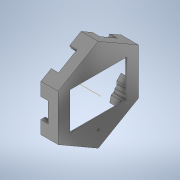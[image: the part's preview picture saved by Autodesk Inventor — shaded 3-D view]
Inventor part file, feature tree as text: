
AUTODESK INVENTOR PART (.ipt)
format: ipt  version: 2020 (Build 240168000, 168)  size: 441,344 bytes
history: native  units: mm
features: extrude x7, sketch x3, pattern_circular x1, chamfer x1, fillet x1, hole x1
ambient origin geometry x8: Origin, YZ Plane, XZ Plane, XY Plane, X Axis, Y Axis, Z Axis, Center Point
bodies: Body1 (feature_tree)
feature tree (14):
  sketch  "Sketch6"  dims[d44=97.0mm d72=6.5mm]
  extrude  "Fronte"  Depth=6.5mm
  extrude  "Esterno"  Depth=1.0mm TaperAngle=0.0deg
  extrude  "Strip"  Depth=6.5mm
  extrude  "Passacavi"  Depth=30.0mm
  extrude  "ScavoStrip"  Depth=2.0mm
  extrude  "ScreenDist0.8"  Depth=2.0mm
  extrude  "SupportoViti"  Depth=2.0mm
  pattern_circular  "RipetizioneSupports"  [2 undecoded]
  chamfer  "Smusso interno"  Distance=2.5mm
  fillet  "RaccordoSupports"  Radius=26.0mm
  hole  "ForoPulsante"  [1 undecoded]
  sketch  "Sketch7"  dims[d77=140.0mm d85=1.0mm d86=0.0mm]
  sketch  "Sketch9"  dims[d87=15.0mm d88=6.5mm d89=30.0mm d91=2.0mm d92=2.0mm d95=1.25mm d96=26.0mm d97=2.5mm d98=26.0mm d99=135.0deg d100=0.0mm d101=25.0mm d102=0.0mm d103=10.0mm d104=0.0mm d105=11.0mm d106=0.0mm d107=5.0mm d108=0.0mm d111=0.8mm d112=0.0mm d114=1.7mm d115=23.0mm d116=0.0mm d117=3.0mm d118=60.0mm d119=360.0deg d121=3.0mm d123=6.0mm d124=85.8mm d125=1.0mm d126=2.0mm d127=45.0deg d128=1.0mm d132=20.0mm d133=18.0mm d135=3.0mm d136=6.0mm d137=7.0mm d138=2.0mm d139=90.0deg d140=8.0mm d141=20.594885mm]
note: 3 required parameter values undecoded (feature->parameter linkage not recoverable at this tier; creation-order binding heuristic only, values carry confidence <= 0.55)
